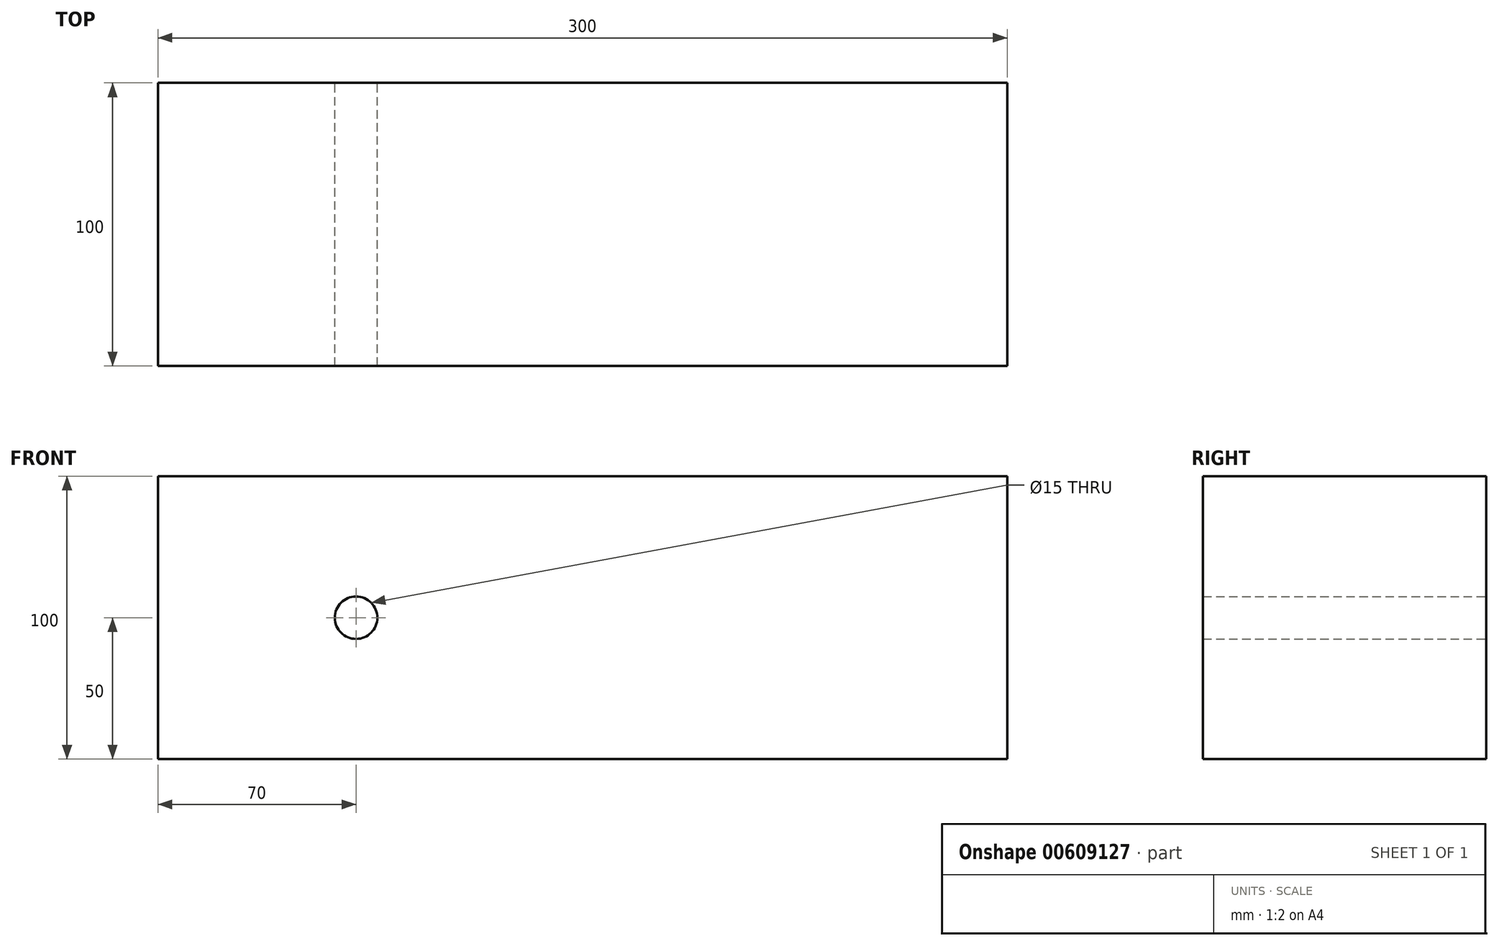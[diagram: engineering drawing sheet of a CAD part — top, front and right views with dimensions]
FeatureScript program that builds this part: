
annotation { "Feature Type Name" : "Feature", "Feature Type Description" : "" }
export const myFeature = defineFeature(function(context is Context, id is Id, definition is map)
    precondition{}
    {
        {
            var Q0;
            Q0=qCreatedBy(makeId("Front.planeOp"),FACE);
            var sketch = newSketch(context, id + "F0", { "sketchPlane" : qUnion([Q0])});
            skLineSegment(sketch, "E0.bottom", {"start": v(-150, 50) * mm, "end": v(150, 50) * mm});
            skLineSegment(sketch, "E0.top", {"start": v(-150, -50) * mm, "end": v(150, -50) * mm});
            skLineSegment(sketch, "E0.left", {"start": v(-150, 50) * mm, "end": v(-150, -50) * mm});
            skLineSegment(sketch, "E0.right", {"start": v(150, 50) * mm, "end": v(150, -50) * mm});
            skCircle(sketch, "E1", {"center": v(-80, 0) * mm, "radius": 7.5 * mm});
            skSolve(sketch);
        }
        {
            var Q0;
            Q0=makeQuery(id+"F0.imprint","IMPRINT",FACE,{"disambiguationData":[TD([[makeQuery(id+"F0.imprint","IMPRINT",EDGE,{"derivedFrom":sQuery(id+"F0.wireOp",EDGE,"E0.bottom")}),-1.0]])]});
            extrude(context, id + "F1", {"entities" : qUnion([Q0]), "depth" : 100 * mm, "offsetDistance" : 25 * mm});
        }
    });
